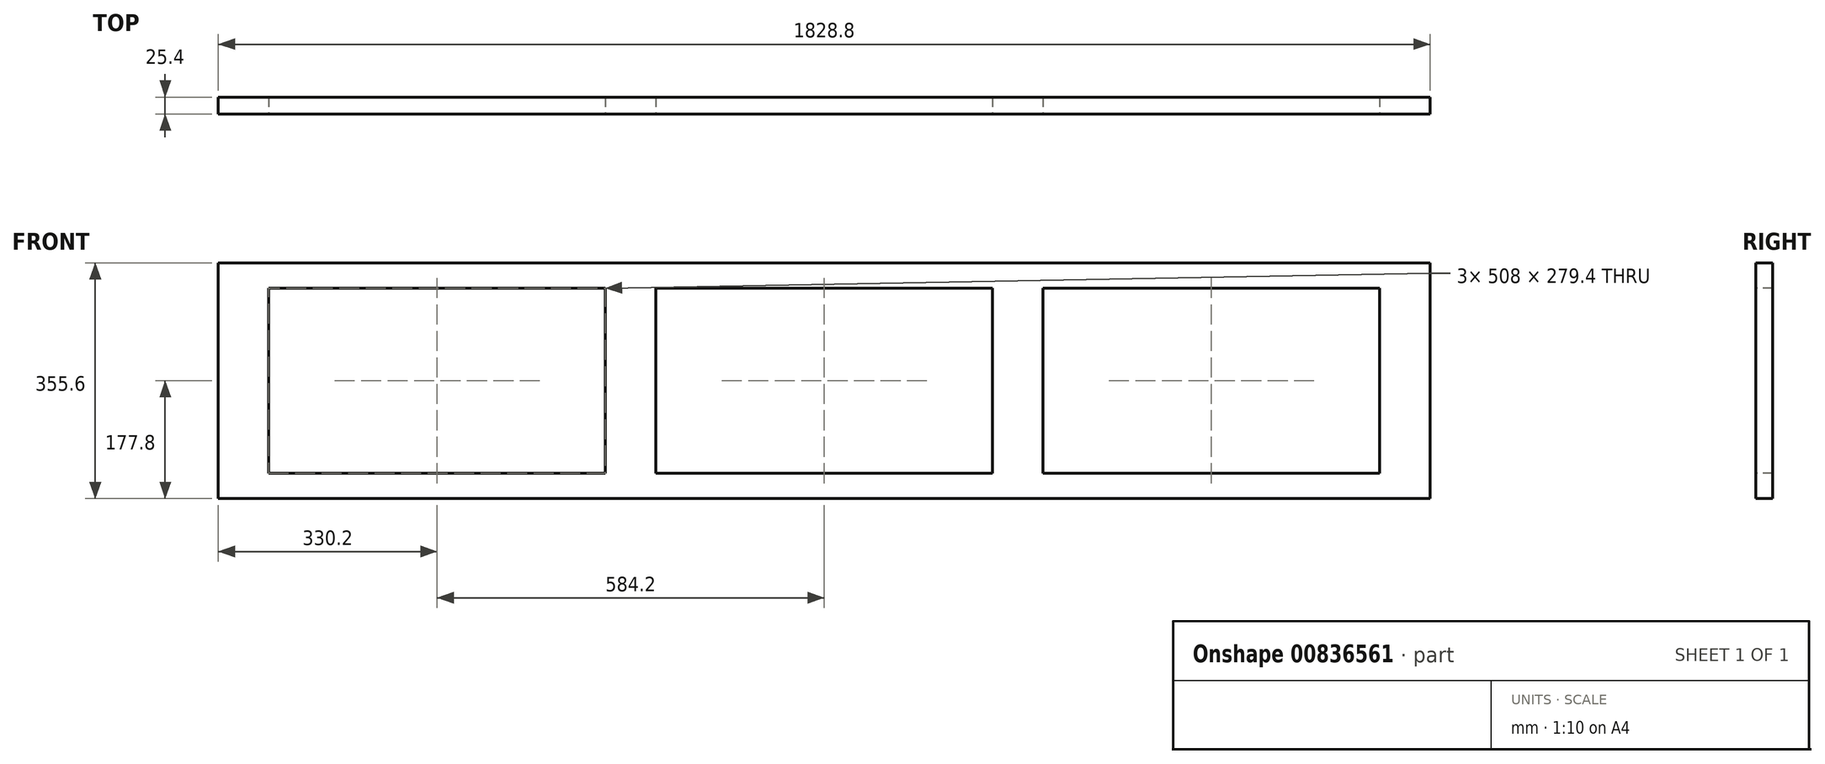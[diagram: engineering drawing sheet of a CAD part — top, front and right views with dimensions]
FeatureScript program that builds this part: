
annotation { "Feature Type Name" : "Feature", "Feature Type Description" : "" }
export const myFeature = defineFeature(function(context is Context, id is Id, definition is map)
    precondition{}
    {
        {
            var Q0;
            Q0=qCreatedBy(makeId("Front.planeOp"),FACE);
            var sketch = newSketch(context, id + "F0", { "sketchPlane" : qUnion([Q0])});
            skLineSegment(sketch, "E0.bottom", {"start": v(0, 0) * mm, "end": v(1828.8, 0) * mm});
            skLineSegment(sketch, "E0.top", {"start": v(0, 355.6) * mm, "end": v(1828.8, 355.6) * mm});
            skLineSegment(sketch, "E0.left", {"start": v(0, 0) * mm, "end": v(0, 355.6) * mm});
            skLineSegment(sketch, "E0.right", {"start": v(1828.8, 0) * mm, "end": v(1828.8, 355.6) * mm});
            skSolve(sketch);
        }
        {
            var Q0;
            Q0=qSketchRegion(id+"F0",true);
            extrude(context, id + "F1", {"entities" : qUnion([Q0]), "depth" : 25.4 * mm, "offsetDistance" : 25.4 * mm});
        }
        {
            var Q0;
            Q0=makeQuery(id+"F1.opExtrude","CAP_FACE",FACE,{"disambiguationData":[OSD([sQuery(id+"F0.wireOp",EDGE,"E0.bottom"),sQuery(id+"F0.wireOp",EDGE,"E0.top"),sQuery(id+"F0.wireOp",EDGE,"E0.left"),sQuery(id+"F0.wireOp",EDGE,"E0.right")])],"isStart":false});
            var sketch = newSketch(context, id + "F2", { "sketchPlane" : qUnion([Q0])});
            skLineSegment(sketch, "E1.bottom", {"start": v(76.2, 317.5) * mm, "end": v(584.2, 317.5) * mm});
            skLineSegment(sketch, "E1.top", {"start": v(76.2, 38.1) * mm, "end": v(584.2, 38.1) * mm});
            skLineSegment(sketch, "E1.left", {"start": v(76.2, 317.5) * mm, "end": v(76.2, 38.1) * mm});
            skLineSegment(sketch, "E1.right", {"start": v(584.2, 317.5) * mm, "end": v(584.2, 38.1) * mm});
            skLineSegment(sketch, "E2.bottom", {"start": v(660.4, 317.5) * mm, "end": v(1168.4, 317.5) * mm});
            skLineSegment(sketch, "E2.top", {"start": v(660.4, 38.1) * mm, "end": v(1168.4, 38.1) * mm});
            skLineSegment(sketch, "E2.left", {"start": v(660.4, 317.5) * mm, "end": v(660.4, 38.1) * mm});
            skLineSegment(sketch, "E2.right", {"start": v(1168.4, 317.5) * mm, "end": v(1168.4, 38.1) * mm});
            skLineSegment(sketch, "E3.bottom", {"start": v(1244.6, 317.5) * mm, "end": v(1752.6, 317.5) * mm});
            skLineSegment(sketch, "E3.top", {"start": v(1244.6, 38.1) * mm, "end": v(1752.6, 38.1) * mm});
            skLineSegment(sketch, "E3.left", {"start": v(1244.6, 317.5) * mm, "end": v(1244.6, 38.1) * mm});
            skLineSegment(sketch, "E3.right", {"start": v(1752.6, 317.5) * mm, "end": v(1752.6, 38.1) * mm});
            skLineSegment(sketch, "E4", {"start": v(584.2, 177.8) * mm, "end": v(660.4, 177.8) * mm, "construction": true});
            skLineSegment(sketch, "E5", {"start": v(1168.4, 177.8) * mm, "end": v(1244.6, 177.8) * mm, "construction": true});
            skSolve(sketch);
        }
        {
            var Q0;
            Q0=qSketchRegion(id+"F2",true);
            extrude(context, id + "F3", {"entities" : qUnion([Q0]), "operationType" : NewBodyOperationType.REMOVE, "oppositeDirection" : true, "depth" : 25.4 * mm, "offsetDistance" : 25.4 * mm});
        }
    });
